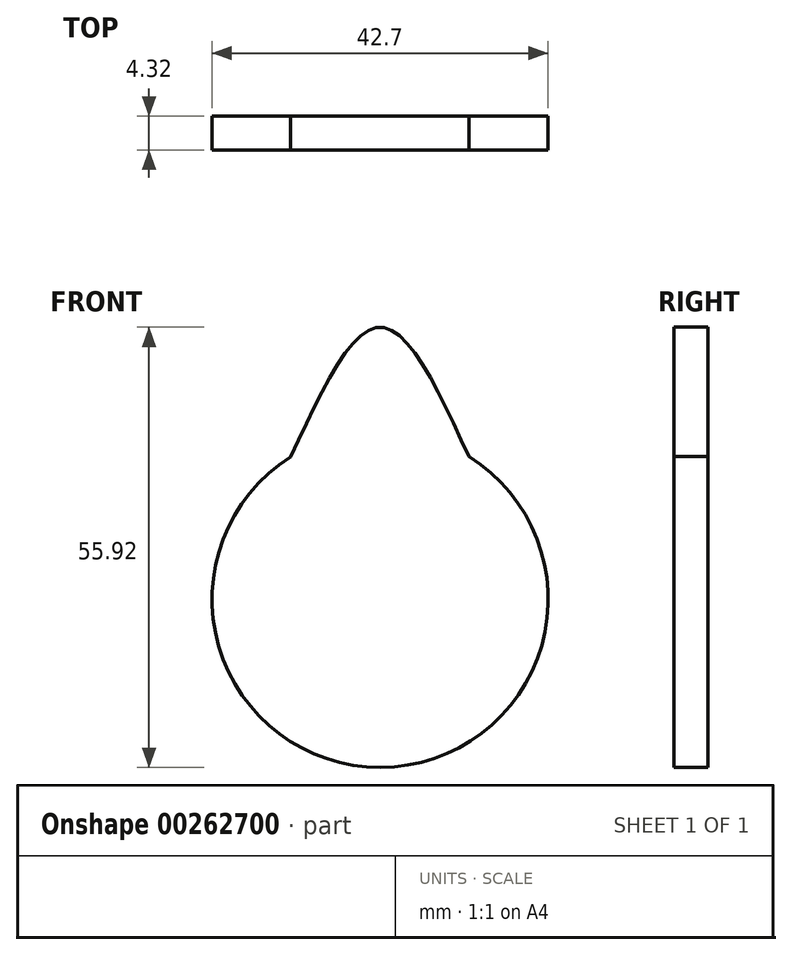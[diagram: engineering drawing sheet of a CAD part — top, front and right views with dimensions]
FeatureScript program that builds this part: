
annotation { "Feature Type Name" : "Feature", "Feature Type Description" : "" }
export const myFeature = defineFeature(function(context is Context, id is Id, definition is map)
    precondition{}
    {
        {
            var Q0;
            Q0=qCreatedBy(makeId("Front.planeOp"),FACE);
            var sketch = newSketch(context, id + "F0", { "sketchPlane" : qUnion([Q0])});
            skCircle(sketch, "E0", {"center": v(0, 0) * mm, "radius": 21.35 * mm});
            skFitSpline(sketch, "E1", {"points": [v(-11.35, 18.08) * mm, v(0, 34.57) * mm, v(11.27, 18.13) * mm], "startDerivative": vector(22.69, 49.47) * mm, "endDerivative": vector(22.52, -49.4) * mm});
            skSolve(sketch);
        }
        {
            var Q0;
            {var subQ0=sQuery(id+"F0.wireOp",EDGE,"E1");var subQ1=sQuery(id+"F0.wireOp",EDGE,"E0");var subQ2=makeQuery(id+"F0.imprint","INTERSECT",VERTEX,{"disambiguationData":[OD(0.0)],"derivedFrom":[subQ1,subQ0]});Q0=makeQuery(id+"F0.imprint","IMPRINT",FACE,{"disambiguationData":[TD([[makeQuery(id+"F0.imprint","IMPRINT",EDGE,{"disambiguationData":[TD([[subQ2,1.0]])],"derivedFrom":subQ1}),1.0]])]});}
            var Q1;
            {var subQ0=sQuery(id+"F0.wireOp",EDGE,"E1");Q1=makeQuery(id+"F0.imprint","IMPRINT",FACE,{"disambiguationData":[TD([[makeQuery(id+"F0.imprint","IMPRINT",EDGE,{"derivedFrom":subQ0}),-1.0]])]});}
            extrude(context, id + "F1", {"entities" : qUnion([Q0, Q1]), "depth" : 4.32 * mm, "offsetDistance" : 25.4 * mm});
        }
    });
